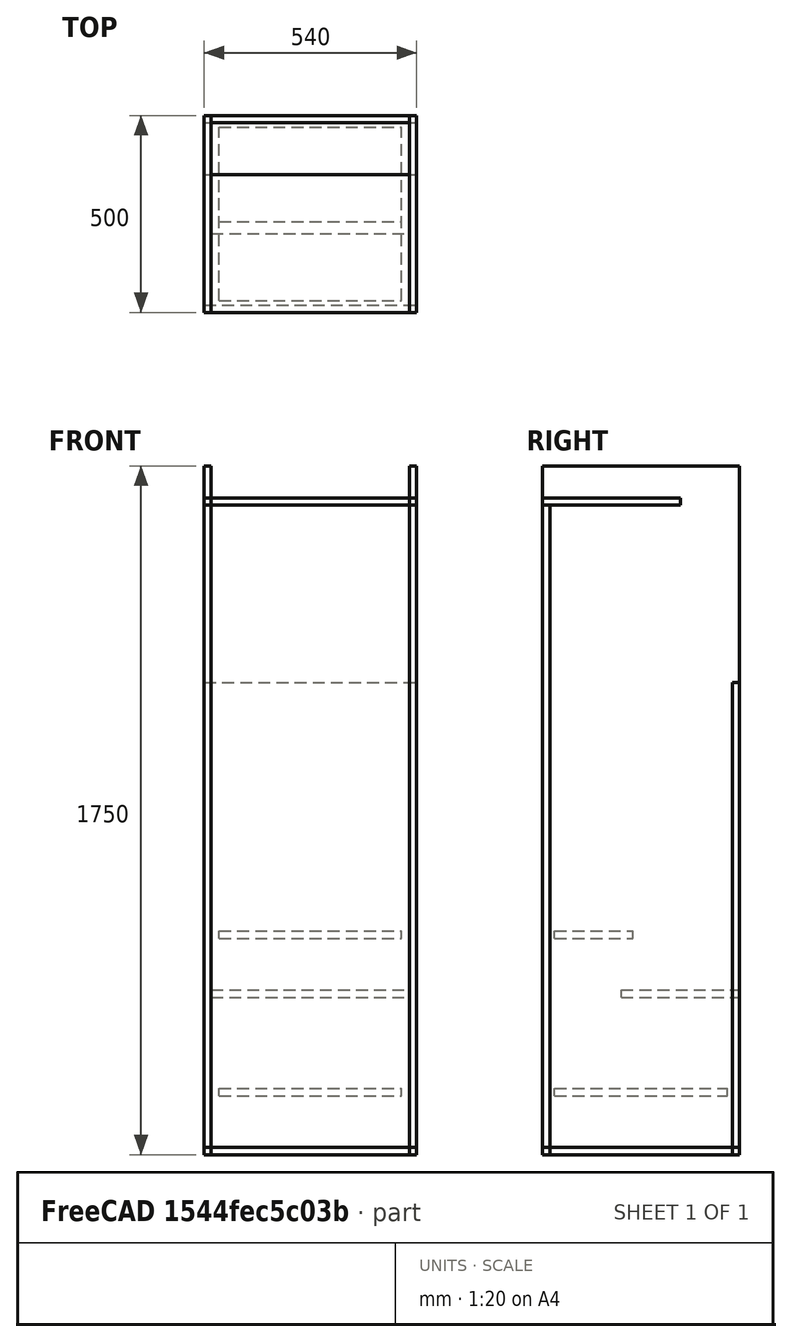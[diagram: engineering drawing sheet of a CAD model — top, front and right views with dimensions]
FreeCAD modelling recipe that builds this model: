
FCSTD DOCUMENT  (FreeCAD 1.0R39319 (Git))
Label: ARTIFACT_Cabinet
License: All rights reserved
LicenseURL: https://en.wikipedia.org/wiki/All_rights_reserved
objects: Part::Box×9
note: 9 computed .brp shape members not serialized (recipe doc carries the construction recipe); baked Part::Feature solids carry a one-line shape summary decoded from their .brp

FEATURE [Part::Box] Box
  AttacherType = Attacher::AttachEngine3D
  Height = 1750
  Length = 18
  Width = 500
FEATURE [Part::Box] Box001
  AttacherType = Attacher::AttachEngine3D
  Height = 1750
  Length = 18
  Placement = pos=(522,0,0) rot=(0,0,1;0rad)
  Width = 500
FEATURE [Part::Box] Box002
  AttacherType = Attacher::AttachEngine3D
  Height = 18
  Length = 540
  Width = 500
FEATURE [Part::Box] Box003
  AttacherType = Attacher::AttachEngine3D
  Height = 1650
  Length = 540
  Width = 18
FEATURE [Part::Box] Box004
  AttacherType = Attacher::AttachEngine3D
  Height = 1200
  Length = 540
  Placement = pos=(0,482,0) rot=(0,0,1;0rad)
  Width = 18
FEATURE [Part::Box] Box005
  AttacherType = Attacher::AttachEngine3D
  Height = 18
  Length = 504
  Placement = pos=(18,200,400) rot=(0,0,1;0rad)
  Width = 300
FEATURE [Part::Box] Box006
  AttacherType = Attacher::AttachEngine3D
  Height = 18
  Length = 464
  Placement = pos=(38,30,150) rot=(0,0,1;0rad)
  Width = 440
FEATURE [Part::Box] Box007
  AttacherType = Attacher::AttachEngine3D
  Height = 18
  Length = 464
  Placement = pos=(38,30,550) rot=(0,0,1;0rad)
  Width = 200
FEATURE [Part::Box] Box008
  AttacherType = Attacher::AttachEngine3D
  Height = 18
  Length = 540
  Placement = pos=(0,0,1650) rot=(0,0,1;0rad)
  Width = 350
